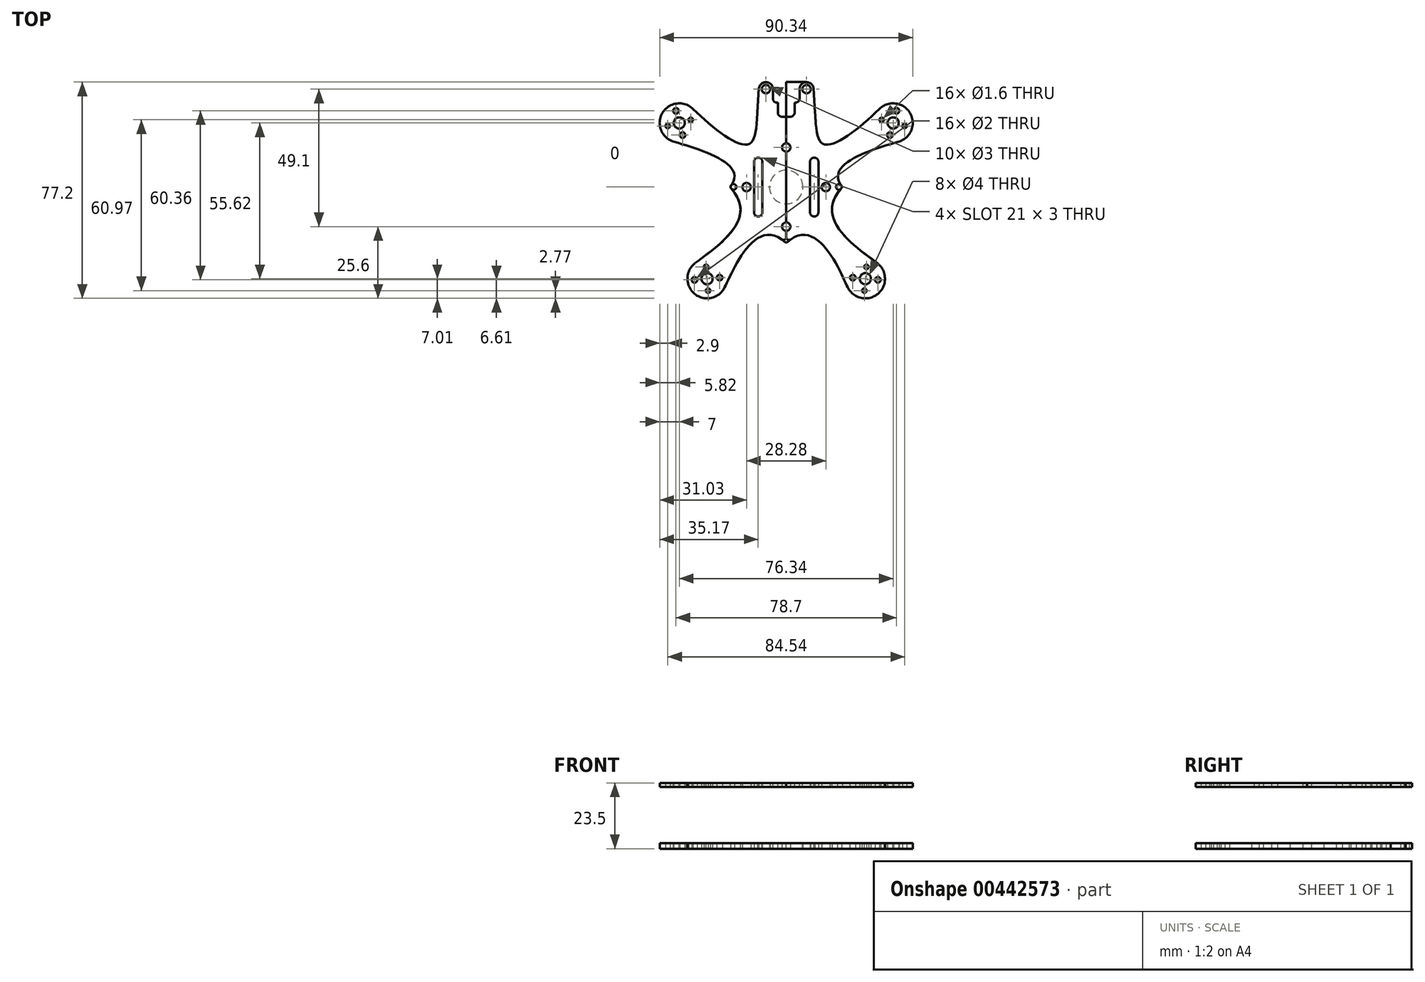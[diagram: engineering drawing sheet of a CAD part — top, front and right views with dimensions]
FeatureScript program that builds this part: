
annotation { "Feature Type Name" : "Feature", "Feature Type Description" : "" }
export const myFeature = defineFeature(function(context is Context, id is Id, definition is map)
    precondition{}
    {
        {
            var Q0;
            Q0=qCreatedBy(makeId("Top.planeOp"),FACE);
            var sketch = newSketch(context, id + "F0", { "sketchPlane" : qUnion([Q0])});
            skCircle(sketch, "E0", {"center": v(0, 0) * mm, "radius": 44 * mm, "construction": true});
            skCircle(sketch, "E1", {"center": v(-38.17, 21.89) * mm, "radius": 27.5 * mm, "construction": true});
            skCircle(sketch, "E2", {"center": v(-28.25, -33.73) * mm, "radius": 27.5 * mm, "construction": true});
            skLineSegment(sketch, "E3", {"start": v(0, -1) * mm, "end": v(-9.55, 8.55) * mm, "construction": true});
            skLineSegment(sketch, "E4", {"start": v(-9.55, 8.55) * mm, "end": v(-19.1, -1) * mm, "construction": true});
            skLineSegment(sketch, "E5", {"start": v(-19.1, -1) * mm, "end": v(0, -20.1) * mm, "construction": true});
            skLineSegment(sketch, "E6", {"start": v(0, -20.1) * mm, "end": v(19.1, -1) * mm, "construction": true});
            skLineSegment(sketch, "E7", {"start": v(19.1, -1) * mm, "end": v(0, 18.1) * mm, "construction": true});
            skLineSegment(sketch, "E8", {"start": v(0, 18.1) * mm, "end": v(-9.55, 8.55) * mm, "construction": true});
            skCircle(sketch, "E9.MirrorC", {"center": v(38.17, 21.89) * mm, "radius": 27.5 * mm, "construction": true});
            skCircle(sketch, "E10.MirrorC", {"center": v(28.25, -33.73) * mm, "radius": 27.5 * mm, "construction": true});
            skLineSegment(sketch, "E11.bottom", {"start": v(9.5, 18.46) * mm, "end": v(-9.5, 18.46) * mm, "construction": true});
            skLineSegment(sketch, "E11.top", {"start": v(9.5, 36.46) * mm, "end": v(-7.25, 36.46) * mm, "construction": true});
            skLineSegment(sketch, "E11.left", {"start": v(9.5, 18.46) * mm, "end": v(9.5, 36.46) * mm, "construction": true});
            skLineSegment(sketch, "E11.right", {"start": v(-9.5, 18.46) * mm, "end": v(-9.5, 36.46) * mm, "construction": true});
            skPoint(sketch, "E11.middle", {"position": v(0, 27.46) * mm});
            skLineSegment(sketch, "E12", {"start": v(0, 0) * mm, "end": v(-38.17, 21.89) * mm, "construction": true});
            skLineSegment(sketch, "E13", {"start": v(0, 0) * mm, "end": v(-28.25, -33.73) * mm, "construction": true});
            skArc(sketch, "E14", {"start": v(-33.24, 26.86) * mm, "mid": v(-44.22, 25.41) * mm, "end": v(-40.07, 15.15) * mm});
            skArc(sketch, "E15", {"start": v(-32.5, -28.17) * mm, "mid": v(-32.69, -39.15) * mm, "end": v(-21.96, -36.81) * mm});
            skLineSegment(sketch, "E16", {"start": v(-19.1, -1) * mm, "end": v(-20.1, -1) * mm, "construction": true});
            skLineSegment(sketch, "E17", {"start": v(0, -20.1) * mm, "end": v(0, -21.1) * mm, "construction": true});
            skFitSpline(sketch, "E18", {"points": [v(-40.07, 15.15) * mm, v(-20.1, -1) * mm], "startDerivative": vector(31.72, -8.95) * mm, "endDerivative": vector(-20.65, -24.15) * mm});
            skFitSpline(sketch, "E19", {"points": [v(-20.1, -1) * mm, v(-32.5, -28.17) * mm], "startDerivative": vector(32.6, -33.84) * mm, "endDerivative": vector(-24.2, -18.5) * mm});
            skFitSpline(sketch, "E20", {"points": [v(-21.96, -36.81) * mm, v(0, -21.1) * mm], "startDerivative": vector(7.77, 15.87) * mm, "endDerivative": vector(32.92, -32.55) * mm});
            skLineSegment(sketch, "E21", {"start": v(-20.82, 11.94) * mm, "end": v(-22.8, 8.47) * mm, "construction": true});
            skLineSegment(sketch, "E22", {"start": v(-15.4, -18.4) * mm, "end": v(-18.48, -15.83) * mm, "construction": true});
            skLineSegment(sketch, "E23", {"start": v(-15.4, -18.4) * mm, "end": v(-12.34, -20.97) * mm, "construction": true});
            skLineSegment(sketch, "E24", {"start": v(-20.82, 11.94) * mm, "end": v(-18.83, 15.4) * mm, "construction": true});
            skFitSpline(sketch, "E25", {"points": [v(-33.24, 26.86) * mm, v(-13.5, 14.3) * mm, v(-9.5, 36.46) * mm], "startDerivative": vector(39.69, -39.3) * mm, "endDerivative": vector(8.23, 68.75) * mm});
            skLineSegment(sketch, "E26", {"start": v(0, 36.46) * mm, "end": v(-9.5, 36.46) * mm});
            skArc(sketch, "E27.filletArc", {"start": v(-7.25, 36.46) * mm, "mid": v(-8.94, 35.8) * mm, "end": v(-9.74, 34.2) * mm});
            skLineSegment(sketch, "E28", {"start": v(0, 36.46) * mm, "end": v(0, -21.1) * mm});
            skCircle(sketch, "E29", {"center": v(0, 13.14) * mm, "radius": 1.5 * mm});
            skLineSegment(sketch, "E30", {"start": v(0, -1) * mm, "end": v(-14.14, -1) * mm, "construction": true});
            skCircle(sketch, "E31", {"center": v(-14.14, -1) * mm, "radius": 1.5 * mm});
            skCircle(sketch, "E32", {"center": v(0, -15.14) * mm, "radius": 1.5 * mm});
            skCircle(sketch, "E33", {"center": v(-38.17, 21.89) * mm, "radius": 2 * mm});
            skLineSegment(sketch, "E34", {"start": v(-38.17, 21.89) * mm, "end": v(-34.07, 23) * mm, "construction": true});
            skCircle(sketch, "E35", {"center": v(-34.07, 23) * mm, "radius": 0.8 * mm});
            skLineSegment(sketch, "E36", {"start": v(-38.17, 21.89) * mm, "end": v(-31.65, 23.66) * mm, "construction": true});
            skLineSegment(sketch, "E37", {"start": v(-38.17, 21.89) * mm, "end": v(-42.27, 20.78) * mm, "construction": true});
            skCircle(sketch, "E38", {"center": v(-42.27, 20.78) * mm, "radius": 0.8 * mm});
            skLineSegment(sketch, "E39", {"start": v(-38.17, 21.89) * mm, "end": v(-39.35, 26.23) * mm, "construction": true});
            skCircle(sketch, "E40", {"center": v(-39.35, 26.23) * mm, "radius": 1 * mm});
            skLineSegment(sketch, "E41", {"start": v(-38.17, 21.89) * mm, "end": v(-37, 17.55) * mm, "construction": true});
            skCircle(sketch, "E42", {"center": v(-37, 17.55) * mm, "radius": 1 * mm});
            skCircle(sketch, "E43", {"center": v(-28.25, -33.73) * mm, "radius": 2 * mm});
            skLineSegment(sketch, "E44", {"start": v(-28.25, -33.73) * mm, "end": v(-28.62, -29.5) * mm, "construction": true});
            skCircle(sketch, "E45", {"center": v(-28.62, -29.5) * mm, "radius": 0.8 * mm});
            skLineSegment(sketch, "E46", {"start": v(-28.25, -33.73) * mm, "end": v(-27.88, -37.97) * mm, "construction": true});
            skCircle(sketch, "E47", {"center": v(-27.88, -37.97) * mm, "radius": 0.8 * mm});
            skLineSegment(sketch, "E48", {"start": v(-28.25, -33.73) * mm, "end": v(-32.73, -34.13) * mm, "construction": true});
            skLineSegment(sketch, "E49", {"start": v(-28.25, -33.73) * mm, "end": v(-23.77, -33.34) * mm, "construction": true});
            skCircle(sketch, "E50", {"center": v(-32.73, -34.13) * mm, "radius": 1 * mm});
            skCircle(sketch, "E51", {"center": v(-23.77, -33.34) * mm, "radius": 1 * mm});
            skLineSegment(sketch, "E52", {"start": v(-10, 8) * mm, "end": v(-10, -10) * mm, "construction": true});
            skArc(sketch, "E53.0.startCap", {"start": v(-11.5, 8) * mm, "mid": v(-10, 9.5) * mm, "end": v(-8.5, 8) * mm});
            skArc(sketch, "E53.0.endCap", {"start": v(-8.5, -10) * mm, "mid": v(-10, -11.5) * mm, "end": v(-11.5, -10) * mm});
            skLineSegment(sketch, "E53.0.left", {"start": v(-8.5, 8) * mm, "end": v(-8.5, -10) * mm});
            skLineSegment(sketch, "E53.0.right", {"start": v(-11.5, 8) * mm, "end": v(-11.5, -10) * mm});
            skCircle(sketch, "E54", {"center": v(0, -1) * mm, "radius": 6 * mm});
            skCircle(sketch, "E55", {"center": v(-7.25, 33.96) * mm, "radius": 1.5 * mm});
            skLineSegment(sketch, "E56", {"start": v(-11.68, 4.78) * mm, "end": v(-9.74, 34.2) * mm});
            skFitSpline(sketch, "E57", {"points": [v(-12.5, -7.6) * mm, v(0, -21.1) * mm], "startDerivative": vector(15.99, -6.1) * mm, "endDerivative": vector(10.3, -23.17) * mm});
            skArc(sketch, "E58", {"start": v(-14.8, -3.93) * mm, "mid": v(-17.14, -0.8) * mm, "end": v(-14.4, 1.99) * mm});
            skArc(sketch, "E59.filletArc", {"start": v(-14.4, 1.99) * mm, "mid": v(-12.53, 2.88) * mm, "end": v(-11.68, 4.78) * mm});
            skLineSegment(sketch, "E60", {"start": v(-12.46, -7.05) * mm, "end": v(-12.48, -7.23) * mm});
            skPoint(sketch, "E61.visualSharp", {"position": v(-12.22, -3.3) * mm});
            skArc(sketch, "E61.filletArc", {"start": v(-12.46, -7.05) * mm, "mid": v(-13.05, -5.06) * mm, "end": v(-14.8, -3.93) * mm});
            skArc(sketch, "E62.filletArc", {"start": v(-12.48, -7.23) * mm, "mid": v(-12.4, -7.53) * mm, "end": v(-12.16, -7.72) * mm});
            skSolve(sketch);
        }
        {
            var Q0;
            Q0=makeQuery(id+"F0.imprint","IMPRINT",FACE,{"disambiguationData":[TD([[makeQuery(id+"F0.imprint","IMPRINT",EDGE,{"derivedFrom":sQuery(id+"F0.wireOp",EDGE,"E14")}),1.0]])]});
            var Q1;
            {var subQ23=sQuery(id+"F0.wireOp",EDGE,"E27.filletArc");Q1=makeQuery(id+"F0.imprint","IMPRINT",FACE,{"disambiguationData":[TD([[makeQuery(id+"F0.imprint","IMPRINT",EDGE,{"derivedFrom":subQ23}),1.0]])]});}
            var Q2;
            Q2=makeQuery(id+"F0.imprint","IMPRINT",FACE,{"disambiguationData":[TD([[makeQuery(id+"F0.imprint","IMPRINT",EDGE,{"derivedFrom":sQuery(id+"F0.wireOp",EDGE,"E31")}),-1.0]])]});
            extrude(context, id + "F1", {"entities" : qUnion([Q0, Q1, Q2]), "depth" : 2 * mm});
        }
        {
            var Q0;
            Q0=makeQuery(id+"F1.opExtrude","SWEPT_EDGE",EDGE,{"disambiguationData":[OSD([sQuery(id+"F0.wireOp",EDGE,"E18"),sQuery(id+"F0.wireOp",EDGE,"E19")])]});
            fillet(context, id + "F2", {"entities" : qUnion([Q0]), "radius" : 1 * mm, "tangentPropagation" : true, "allowEdgeOverflow" : false});
        }
        {
            var Q0;
            Q0=makeQuery(id+"F1.opExtrude","SWEPT_BODY",BODY,{"disambiguationData":[OSD([sQuery(id+"F0.wireOp",EDGE,"E14"),sQuery(id+"F0.wireOp",EDGE,"E15"),sQuery(id+"F0.wireOp",EDGE,"E18"),sQuery(id+"F0.wireOp",EDGE,"E19"),sQuery(id+"F0.wireOp",EDGE,"E20"),sQuery(id+"F0.wireOp",EDGE,"E25"),sQuery(id+"F0.wireOp",EDGE,"E26"),sQuery(id+"F0.wireOp",EDGE,"E27.filletArc"),sQuery(id+"F0.wireOp",EDGE,"E28"),sQuery(id+"F0.wireOp",EDGE,"E29"),sQuery(id+"F0.wireOp",EDGE,"E31"),sQuery(id+"F0.wireOp",EDGE,"E32"),sQuery(id+"F0.wireOp",EDGE,"E33"),sQuery(id+"F0.wireOp",EDGE,"E35"),sQuery(id+"F0.wireOp",EDGE,"E38"),sQuery(id+"F0.wireOp",EDGE,"E40"),sQuery(id+"F0.wireOp",EDGE,"E42"),sQuery(id+"F0.wireOp",EDGE,"E43"),sQuery(id+"F0.wireOp",EDGE,"E45"),sQuery(id+"F0.wireOp",EDGE,"E47"),sQuery(id+"F0.wireOp",EDGE,"E50"),sQuery(id+"F0.wireOp",EDGE,"E51"),sQuery(id+"F0.wireOp",EDGE,"E53.0.startCap"),sQuery(id+"F0.wireOp",EDGE,"E53.0.endCap"),sQuery(id+"F0.wireOp",EDGE,"E53.0.left"),sQuery(id+"F0.wireOp",EDGE,"E53.0.right"),sQuery(id+"F0.wireOp",EDGE,"E54"),sQuery(id+"F0.wireOp",EDGE,"E55")])]});
            var Q1;
            {var subQ0=sQuery(id+"F0.wireOp",EDGE,"E28");Q1=makeQuery(id+"F1.opExtrude","SWEPT_FACE",FACE,{"disambiguationData":[OSD([subQ0]),TDD([makeQuery(id+"F0.imprint","IMPRINT",EDGE,{"disambiguationData":[TD([[makeQuery(id+"F0.imprint","INTERSECT",VERTEX,{"derivedFrom":[sQuery(id+"F0.wireOp",EDGE,"E26"),subQ0]}),-1.0]])],"derivedFrom":subQ0})])]});}
            mirror(context, id + "F3", {"operationType" : NewBodyOperationType.ADD, "entities" : qUnion([Q0]), "mirrorPlane" : qUnion([Q1])});
        }
        {
            var Q0;
            {var subQ23=sQuery(id+"F0.wireOp",EDGE,"E27.filletArc");Q0=makeQuery(id+"F0.imprint","IMPRINT",FACE,{"disambiguationData":[TD([[makeQuery(id+"F0.imprint","IMPRINT",EDGE,{"derivedFrom":subQ23}),1.0]])]});}
            var Q1;
            Q1=makeQuery(id+"F0.imprint","IMPRINT",FACE,{"disambiguationData":[TD([[makeQuery(id+"F0.imprint","IMPRINT",EDGE,{"derivedFrom":sQuery(id+"F0.wireOp",EDGE,"E31")}),-1.0]])]});
            var Q2;
            {var subQ1=sQuery(id+"F0.wireOp",EDGE,"E53.0.startCap");var subQ5=sQuery(id+"F0.wireOp",EDGE,"E53.0.left");var subQ6=makeQuery(id+"F0.imprint","INTERSECT",VERTEX,{"derivedFrom":[subQ1,subQ5]});Q2=makeQuery(id+"F0.imprint","IMPRINT",FACE,{"disambiguationData":[TD([[makeQuery(id+"F0.imprint","IMPRINT",EDGE,{"disambiguationData":[TD([[subQ6,1.0]])],"derivedFrom":subQ1}),-1.0]])]});}
            var Q3;
            {var subQ0=sQuery(id+"F0.wireOp",EDGE,"E54");var subQ1=sQuery(id+"F0.wireOp",EDGE,"E28");var subQ2=makeQuery(id+"F0.imprint","INTERSECT",VERTEX,{"disambiguationData":[OD(0.0)],"derivedFrom":[subQ1,subQ0]});Q3=makeQuery(id+"F0.imprint","IMPRINT",FACE,{"disambiguationData":[TD([[makeQuery(id+"F0.imprint","IMPRINT",EDGE,{"disambiguationData":[TD([[subQ2,-1.0]])],"derivedFrom":subQ1}),-1.0]])]});}
            var Q4;
            {var subQ0=sQuery(id+"F0.wireOp",EDGE,"E29");var subQ1=sQuery(id+"F0.wireOp",EDGE,"E28");var subQ2=makeQuery(id+"F0.imprint","INTERSECT",VERTEX,{"disambiguationData":[OD(0.0)],"derivedFrom":[subQ1,subQ0]});Q4=makeQuery(id+"F0.imprint","IMPRINT",FACE,{"disambiguationData":[TD([[makeQuery(id+"F0.imprint","IMPRINT",EDGE,{"disambiguationData":[TD([[subQ2,-1.0]])],"derivedFrom":subQ1}),-1.0]])]});}
            extrude(context, id + "F4", {"entities" : qUnion([Q0, Q1, Q2, Q3, Q4]), "depth" : 23.5 * mm, "hasSecondDirection" : true, "secondDirectionOppositeDirection" : false, "secondDirectionDepth" : 22 * mm});
        }
        {
            var Q0;
            {var subQ0=makeQuery(id+"F4.opExtrude","CAP_FACE",FACE,{"disambiguationData":[OSD([sQuery(id+"F0.wireOp",EDGE,"E25"),sQuery(id+"F0.wireOp",EDGE,"E26"),sQuery(id+"F0.wireOp",EDGE,"E27.filletArc"),sQuery(id+"F0.wireOp",EDGE,"E28"),sQuery(id+"F0.wireOp",EDGE,"E31"),sQuery(id+"F0.wireOp",EDGE,"E32"),sQuery(id+"F0.wireOp",EDGE,"E55"),sQuery(id+"F0.wireOp",EDGE,"E56"),sQuery(id+"F0.wireOp",EDGE,"E57"),sQuery(id+"F0.wireOp",EDGE,"E58"),sQuery(id+"F0.wireOp",EDGE,"E59.filletArc"),sQuery(id+"F0.wireOp",EDGE,"E60"),sQuery(id+"F0.wireOp",EDGE,"E61.filletArc"),sQuery(id+"F0.wireOp",EDGE,"E62.filletArc")])],"isStart":false});Q0=makeQuery(id+"F7.boolean.opBoolean","MERGE",FACE,{"derivedFrom":[subQ0,makeQuery(id+"F7.opPattern","COPY",FACE,{"derivedFrom":subQ0,"instanceName":"1"})]});}
            var sketch = newSketch(context, id + "F5", { "sketchPlane" : qUnion([Q0])});
            skCircle(sketch, "E63", {"center": v(-7.25, 33.96) * mm, "radius": 2.5 * mm});
            skLineSegment(sketch, "E64", {"start": v(-4.76, 34.1) * mm, "end": v(-4.76, 30.6) * mm});
            skLineSegment(sketch, "E65", {"start": v(-3.26, 29.1) * mm, "end": v(-3, 29.1) * mm});
            skLineSegment(sketch, "E66", {"start": v(-3, 29.1) * mm, "end": v(-3, 25.6) * mm});
            skLineSegment(sketch, "E67", {"start": v(-1.5, 24.1) * mm, "end": v(0, 24.1) * mm});
            skPoint(sketch, "E68.visualSharp", {"position": v(-4.76, 29.1) * mm});
            skArc(sketch, "E68.filletArc", {"start": v(-4.76, 30.6) * mm, "mid": v(-4.32, 29.54) * mm, "end": v(-3.26, 29.1) * mm});
            skPoint(sketch, "E69.visualSharp", {"position": v(-3, 24.1) * mm});
            skArc(sketch, "E69.filletArc", {"start": v(-3, 25.6) * mm, "mid": v(-2.56, 24.54) * mm, "end": v(-1.5, 24.1) * mm});
            skPoint(sketch, "E70.orphan", {"position": v(0, 29.1) * mm});
            skSolve(sketch);
        }
        {
            var Q0;
            Q0=makeQuery(id+"F5.imprint","IMPRINT",FACE,{"disambiguationData":[TD([[makeQuery(id+"F5.imprint","IMPRINT",EDGE,{"derivedFrom":sQuery(id+"F5.wireOp",EDGE,"E65")}),1.0]])]});
            extrude(context, id + "F6", {"entities" : qUnion([Q0]), "operationType" : NewBodyOperationType.REMOVE, "oppositeDirection" : true, "depth" : 25 * mm});
        }
        {
            var Q0;
            Q0=makeQuery(id+"F4.opExtrude","SWEPT_BODY",BODY,{"disambiguationData":[OSD([sQuery(id+"F0.wireOp",EDGE,"E25"),sQuery(id+"F0.wireOp",EDGE,"E26"),sQuery(id+"F0.wireOp",EDGE,"E27.filletArc"),sQuery(id+"F0.wireOp",EDGE,"E28"),sQuery(id+"F0.wireOp",EDGE,"E31"),sQuery(id+"F0.wireOp",EDGE,"E32"),sQuery(id+"F0.wireOp",EDGE,"E55"),sQuery(id+"F0.wireOp",EDGE,"E56"),sQuery(id+"F0.wireOp",EDGE,"E57"),sQuery(id+"F0.wireOp",EDGE,"E58"),sQuery(id+"F0.wireOp",EDGE,"E59.filletArc"),sQuery(id+"F0.wireOp",EDGE,"E60"),sQuery(id+"F0.wireOp",EDGE,"E61.filletArc"),sQuery(id+"F0.wireOp",EDGE,"E62.filletArc")])]});
            var Q1;
            {var subQ0=sQuery(id+"F0.wireOp",EDGE,"E54");var subQ1=sQuery(id+"F0.wireOp",EDGE,"E28");var subQ2=makeQuery(id+"F0.imprint","INTERSECT",VERTEX,{"disambiguationData":[OD(1.0)],"derivedFrom":[subQ1,subQ0]});var subQ3=makeQuery(id+"F0.imprint","INTERSECT",VERTEX,{"disambiguationData":[OD(0.0)],"derivedFrom":[subQ1,subQ0]});var subQ4=sQuery(id+"F0.wireOp",EDGE,"E29");var subQ5=makeQuery(id+"F0.imprint","INTERSECT",VERTEX,{"disambiguationData":[OD(1.0)],"derivedFrom":[subQ1,subQ4]});var subQ6=makeQuery(id+"F0.imprint","INTERSECT",VERTEX,{"disambiguationData":[OD(0.0)],"derivedFrom":[subQ1,subQ4]});Q1=makeQuery(id+"F4.opExtrude","SWEPT_FACE",FACE,{"disambiguationData":[OSD([subQ1]),TDD([makeQuery(id+"F0.imprint","IMPRINT",EDGE,{"disambiguationData":[TD([[makeQuery(id+"F0.imprint","INTERSECT",VERTEX,{"derivedFrom":[sQuery(id+"F0.wireOp",EDGE,"E26"),subQ1]}),-1.0]])],"derivedFrom":subQ1}),makeQuery(id+"F0.imprint","IMPRINT",EDGE,{"disambiguationData":[TD([[subQ6,-1.0]])],"derivedFrom":subQ1}),makeQuery(id+"F0.imprint","IMPRINT",EDGE,{"disambiguationData":[TD([[subQ5,-1.0]])],"derivedFrom":subQ1}),makeQuery(id+"F0.imprint","IMPRINT",EDGE,{"disambiguationData":[TD([[subQ3,-1.0]])],"derivedFrom":subQ1}),makeQuery(id+"F0.imprint","IMPRINT",EDGE,{"disambiguationData":[TD([[subQ2,-1.0]])],"derivedFrom":subQ1})])]});}
            mirror(context, id + "F7", {"operationType" : NewBodyOperationType.ADD, "entities" : qUnion([Q0]), "mirrorPlane" : qUnion([Q1])});
        }
        {
            var Q0;
            {var subQ0=makeQuery(id+"F1.opExtrude","SWEPT_EDGE",EDGE,{"disambiguationData":[OSD([sQuery(id+"F0.wireOp",EDGE,"E20"),sQuery(id+"F0.wireOp",EDGE,"E28")])]});Q0=makeQuery(id+"F3.boolean.opBoolean","MERGE",EDGE,{"derivedFrom":[subQ0,makeQuery(id+"F3.opPattern","COPY",EDGE,{"derivedFrom":subQ0,"instanceName":"1"})]});}
            var Q1;
            {var subQ0=makeQuery(id+"F4.opExtrude","SWEPT_EDGE",EDGE,{"disambiguationData":[OSD([sQuery(id+"F0.wireOp",EDGE,"E20"),sQuery(id+"F0.wireOp",EDGE,"E28"),sQuery(id+"F0.wireOp",EDGE,"E57")])]});Q1=makeQuery(id+"F7.boolean.opBoolean","MERGE",EDGE,{"derivedFrom":[subQ0,makeQuery(id+"F7.opPattern","COPY",EDGE,{"derivedFrom":subQ0,"instanceName":"1"})]});}
            fillet(context, id + "F8", {"entities" : qUnion([Q0, Q1]), "radius" : 1 * mm, "tangentPropagation" : true, "allowEdgeOverflow" : false});
        }
    });
